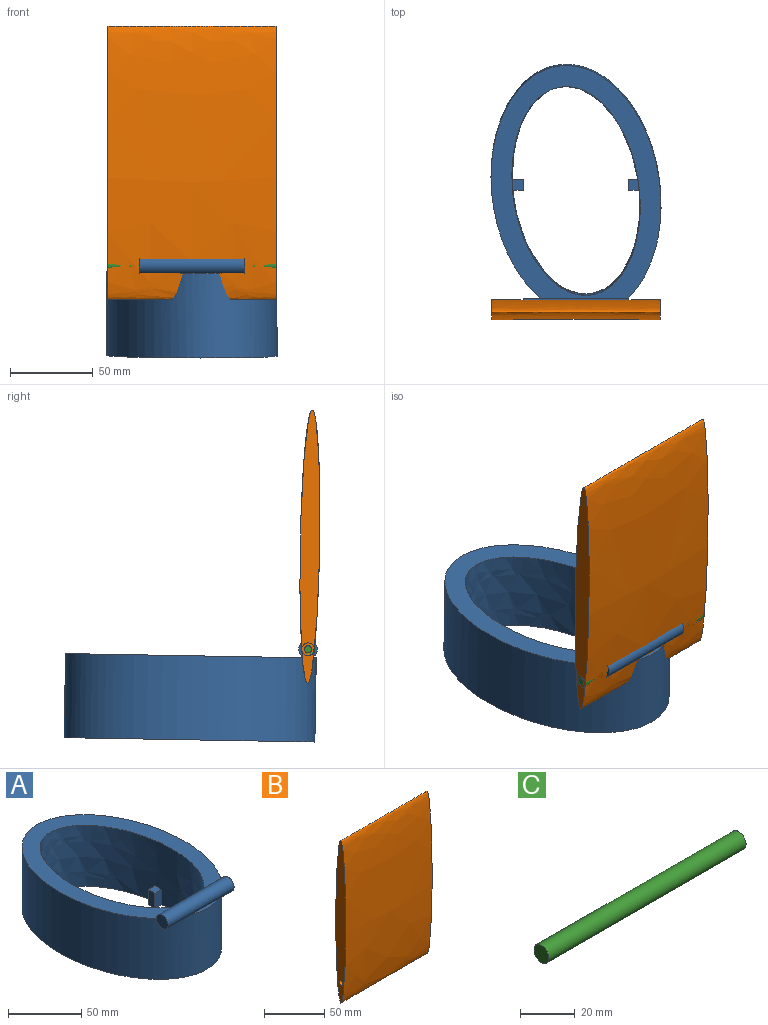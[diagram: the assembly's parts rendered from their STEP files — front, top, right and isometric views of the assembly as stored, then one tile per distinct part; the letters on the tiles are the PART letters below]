
ASSEMBLY  parts=3 mates=2
PART A: 16 faces, bbox 102.8x152x61.5 mm
  f0: extruded ~125.68x77.53mm, area 16307mm2, adj f2,f4,f8,f10,f11,f12,f14,f15
  f1: extruded ~150.95x102.79mm, area 20467.2mm2, adj f2,f3,f4,f5
  f2: plane 144.45x102.8mm, normal (0,0,1), area 4351.9mm2, adj f0,f1,f5
  f3: plane 28.83x3.08mm, normal (0,0,1), area 59.5mm2, adj f1,f5
  f4: plane 151.6x102.8mm, normal (0,0,-1), area 4643.4mm2, adj f0,f1,f9,f10,f11,f13,f14,f15
  f5: cylinder r=5.55mm len=63.5mm, axis (-1,0,0), area 2061.7mm2, adj f1,f2,f3,f6,f7
  f6: plane 11.1x11.1mm, normal (1,0,0), area 96.8mm2, adj f5
  f7: plane 11.1x11.1mm, normal (-1,0,0), area 96.8mm2, adj f5
  f8: plane 6.61x6.35mm, normal (0,0,1), area 39.7mm2, adj f0,f9,f10,f11
  f9: plane 12.7x6.35mm, normal (-1,0,0), area 80.6mm2, adj f4,f8,f10,f11
  f10: plane 12.7x5.82mm, normal (0,1,0), area 74mm2, adj f0,f4,f8,f9
  f11: plane 12.7x6.61mm, normal (0,-1,0), area 83.9mm2, adj f0,f4,f8,f9
  f12: plane 7x6.35mm, normal (0,0,1), area 43.4mm2, adj f0,f13,f14,f15
  f13: plane 12.7x6.35mm, normal (1,0,0), area 80.6mm2, adj f4,f12,f14,f15
  f14: plane 12.7x7mm, normal (0,1,0), area 88.9mm2, adj f0,f4,f12,f13
  f15: plane 12.7x6.61mm, normal (0,-1,0), area 83.9mm2, adj f0,f4,f12,f13
PART B: 4 faces, bbox 101.6x11.8x165.1 mm
  f0: cylinder r=2.18mm len=101.6mm, axis (-1,0,0), area 1391.9mm2, adj f2,f3
  f1: extruded ~165.1x101.6mm, area 33996.2mm2, adj f2,f3
  f2: plane 165.1x11.78mm, normal (1,0,0), area 1512.6mm2, adj f0,f1
  f3: plane 165.1x11.78mm, normal (-1,0,0), area 1512.6mm2, adj f0,f1
PART C: 3 faces, bbox 101.6x7.6x7.6 mm
  f0: cylinder r=3.82mm len=101.6mm, axis (-1,0,0), area 2440.3mm2, adj f1,f2
  f1: plane 7.65x7.65mm, normal (1,0,0), area 45.9mm2, adj f0
  f2: plane 7.65x7.65mm, normal (-1,0,0), area 45.9mm2, adj f0
PLACE A rot(axis=(1,0,0),1deg) t=(148.84,-19.99,-18.66)mm
PLACE B rot(axis=(1,0,0),1deg) t=(148.84,-21.87,-2.27)mm
PLACE C rot(axis=(-1,0,0),89deg) t=(148.84,-130.63,-33.83)mm
MATE revolute B.f0 <-> C.f0  axis (-1,0,0) through (98.04,-91.64,36.06)mm
MATE revolute C.f0 <-> A.f5  axis (-1,0,0) through (148.84,-91.64,36.06)mm
